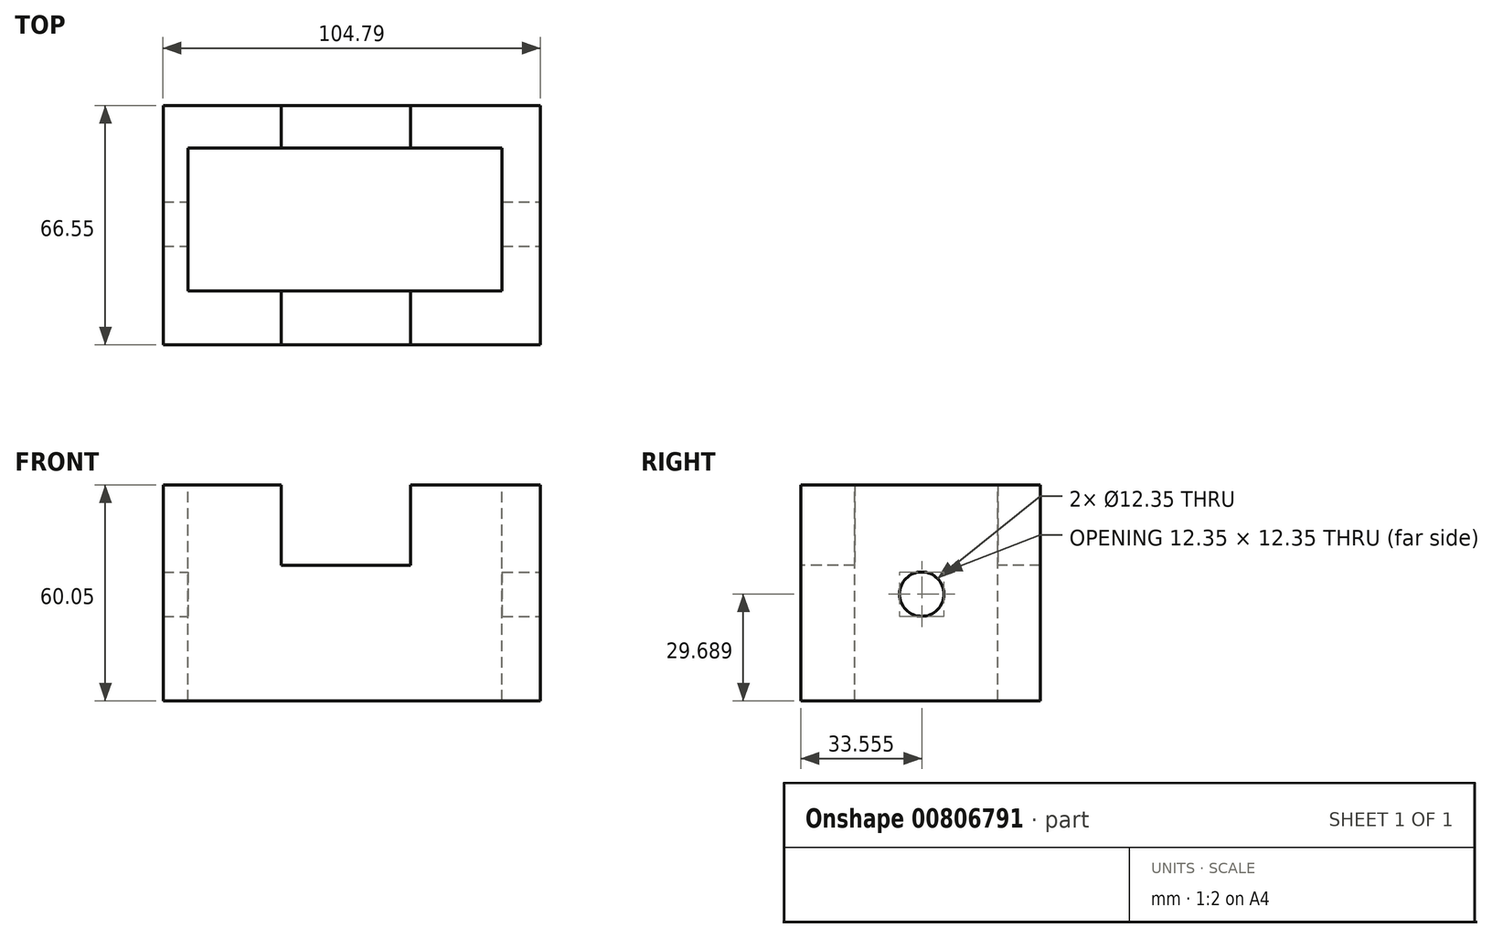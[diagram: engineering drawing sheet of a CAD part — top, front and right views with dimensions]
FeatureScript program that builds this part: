
annotation { "Feature Type Name" : "Feature", "Feature Type Description" : "" }
export const myFeature = defineFeature(function(context is Context, id is Id, definition is map)
    precondition{}
    {
        {
            var Q0;
            Q0=qCreatedBy(makeId("Front.planeOp"),FACE);
            var sketch = newSketch(context, id + "F0", { "sketchPlane" : qUnion([Q0])});
            skLineSegment(sketch, "E0.bottom", {"start": v(-49.99, 29.46) * mm, "end": v(54.8, 29.46) * mm});
            skLineSegment(sketch, "E0.top", {"start": v(-49.99, -30.59) * mm, "end": v(54.8, -30.59) * mm});
            skLineSegment(sketch, "E0.left", {"start": v(-49.99, 29.46) * mm, "end": v(-49.99, -30.59) * mm});
            skLineSegment(sketch, "E0.right", {"start": v(54.8, 29.46) * mm, "end": v(54.8, -30.59) * mm});
            skSolve(sketch);
        }
        {
            var Q0;
            Q0 = qSketchRegion(id + "F0", true);
            extrude(context, id + "F1", {"entities" : qUnion([Q0]), "depth" : 66.55 * mm, "offsetDistance" : 25.4 * mm});
        }
        {
            var Q0;
            Q0=makeQuery(id+"F1.opExtrude","CAP_FACE",FACE,{"disambiguationData":[OSD([sQuery(id+"F0.wireOp",EDGE,"E0.bottom"),sQuery(id+"F0.wireOp",EDGE,"E0.top"),sQuery(id+"F0.wireOp",EDGE,"E0.left"),sQuery(id+"F0.wireOp",EDGE,"E0.right")])],"isStart":false});
            var sketch = newSketch(context, id + "F2", { "sketchPlane" : qUnion([Q0])});
            skLineSegment(sketch, "E1.bottom", {"start": v(-17.13, 29.46) * mm, "end": v(18.83, 29.46) * mm});
            skLineSegment(sketch, "E1.top", {"start": v(-17.13, 7.08) * mm, "end": v(18.83, 7.08) * mm});
            skLineSegment(sketch, "E1.left", {"start": v(-17.13, 29.46) * mm, "end": v(-17.13, 7.08) * mm});
            skLineSegment(sketch, "E1.right", {"start": v(18.83, 29.46) * mm, "end": v(18.83, 7.08) * mm});
            skSolve(sketch);
        }
        {
            var Q0;
            Q0=makeQuery(id+"F1.opExtrude","SWEPT_FACE",FACE,{"disambiguationData":[OSD([sQuery(id+"F0.wireOp",EDGE,"E0.bottom")])]});
            var sketch = newSketch(context, id + "F3", { "sketchPlane" : qUnion([Q0])});
            skLineSegment(sketch, "E2.bottom", {"start": v(-43.06, -11.84) * mm, "end": v(44.23, -11.84) * mm});
            skLineSegment(sketch, "E2.top", {"start": v(-43.06, -51.6) * mm, "end": v(44.23, -51.6) * mm});
            skLineSegment(sketch, "E2.left", {"start": v(-43.06, -11.84) * mm, "end": v(-43.06, -51.6) * mm});
            skLineSegment(sketch, "E2.right", {"start": v(44.23, -11.84) * mm, "end": v(44.23, -51.6) * mm});
            skSolve(sketch);
        }
        {
            var Q0;
            Q0=makeQuery(id+"F3.imprint","IMPRINT",FACE,{"disambiguationData":[TD([[makeQuery(id+"F3.imprint","IMPRINT",EDGE,{"derivedFrom":sQuery(id+"F3.wireOp",EDGE,"E2.bottom")}),-1.0]])]});
            extrude(context, id + "F4", {"entities" : qUnion([Q0]), "operationType" : NewBodyOperationType.REMOVE, "endBound" : BoundingType.THROUGH_ALL, "oppositeDirection" : true, "depth" : 93.22 * mm, "offsetDistance" : 25.4 * mm});
        }
        {
            var Q0;
            Q0=makeQuery(id+"F2.imprint","IMPRINT",FACE,{"disambiguationData":[TD([[makeQuery(id+"F2.imprint","IMPRINT",EDGE,{"derivedFrom":sQuery(id+"F2.wireOp",EDGE,"E1.bottom")}),-1.0]])]});
            extrude(context, id + "F5", {"entities" : qUnion([Q0]), "operationType" : NewBodyOperationType.REMOVE, "endBound" : BoundingType.THROUGH_ALL, "oppositeDirection" : true, "depth" : 25.4 * mm, "offsetDistance" : 25.4 * mm});
        }
        {
            var Q0;
            Q0=makeQuery(id+"F1.opExtrude","SWEPT_FACE",FACE,{"disambiguationData":[OSD([sQuery(id+"F0.wireOp",EDGE,"E0.right")])]});
            var sketch = newSketch(context, id + "F6", { "sketchPlane" : qUnion([Q0])});
            skCircle(sketch, "E3", {"center": v(-33, -0.9) * mm, "radius": 6.17 * mm});
            skSolve(sketch);
        }
        {
            var Q0;
            Q0 = qSketchRegion(id + "F6", true);
            extrude(context, id + "F7", {"entities" : qUnion([Q0]), "operationType" : NewBodyOperationType.REMOVE, "endBound" : BoundingType.THROUGH_ALL, "oppositeDirection" : true, "depth" : 25.4 * mm, "offsetDistance" : 25.4 * mm});
        }
    });
